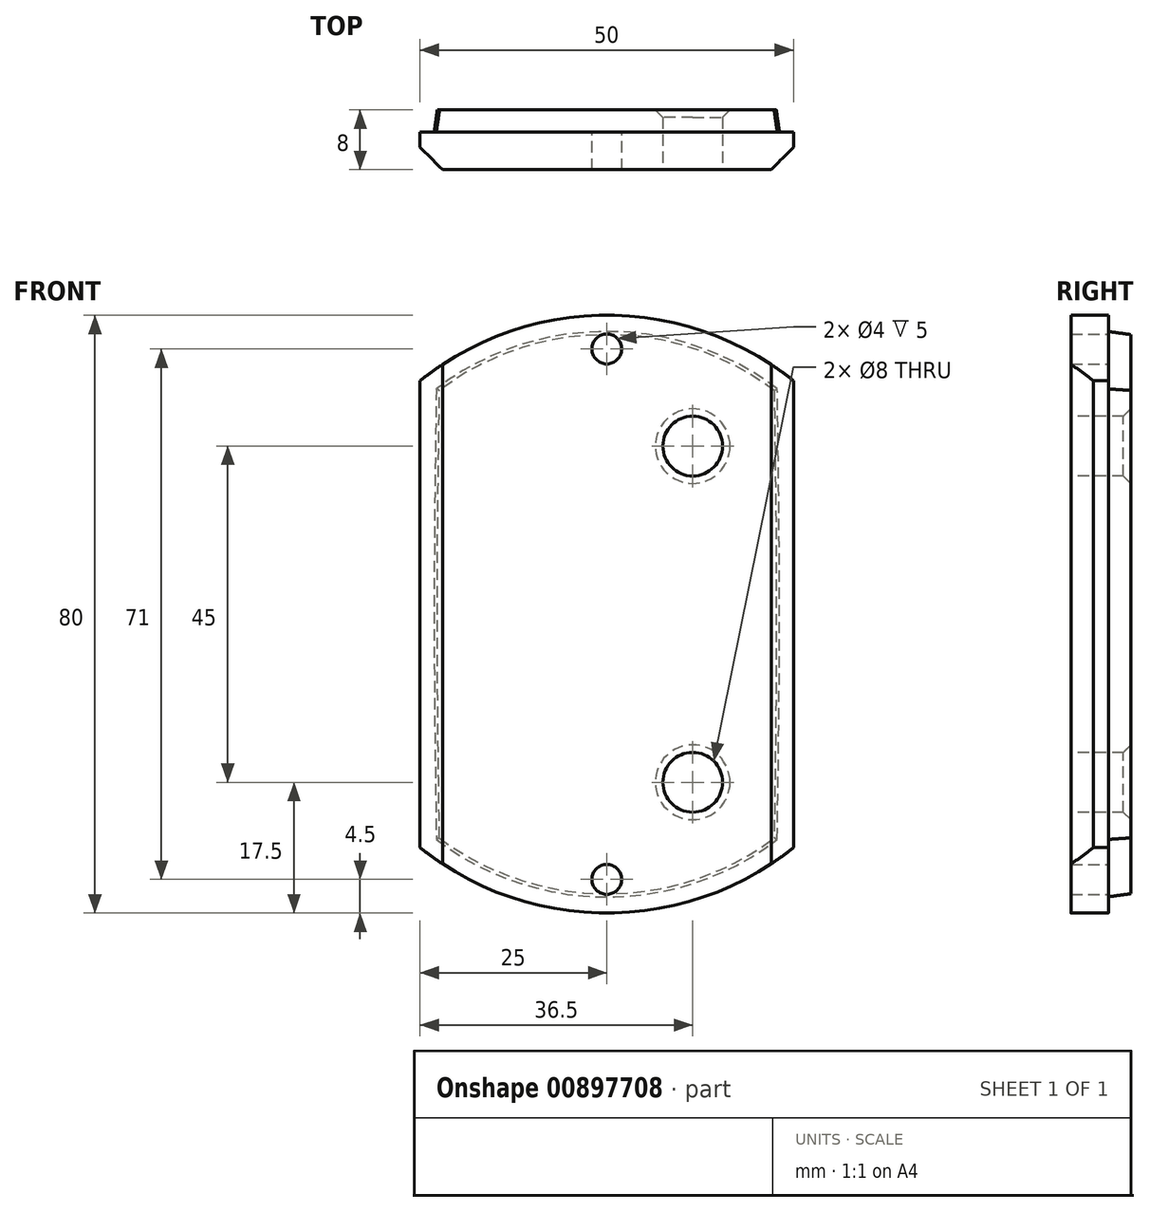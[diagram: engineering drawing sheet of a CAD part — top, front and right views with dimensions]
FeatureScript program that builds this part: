
annotation { "Feature Type Name" : "Feature", "Feature Type Description" : "" }
export const myFeature = defineFeature(function(context is Context, id is Id, definition is map)
    precondition{}
    {
        {
            var Q0;
            Q0=qCreatedBy(makeId("Front.planeOp"),FACE);
            var sketch = newSketch(context, id + "F0", { "sketchPlane" : qUnion([Q0])});
            skFitSpline(sketch, "E0.0", {"points": [v(-22.81, -30.15) * mm, v(-22, -30.77) * mm, v(-20.31, -31.94) * mm, v(-17.68, -33.47) * mm, v(-15.39, -34.57) * mm, v(-13.5, -35.33) * mm, v(-12.05, -35.85) * mm, v(-10.57, -36.32) * mm, v(-8.6, -36.85) * mm, v(-6.11, -37.36) * mm, v(-3.09, -37.73) * mm, v(-0.54, -37.84) * mm, v(1.52, -37.8) * mm, v(3.57, -37.67) * mm, v(6.1, -37.36) * mm, v(9.08, -36.75) * mm, v(12, -35.9) * mm, v(14.9, -34.8) * mm, v(17.67, -33.48) * mm, v(20.31, -31.94) * mm, v(22, -30.77) * mm, v(22.81, -30.15) * mm]});
            skLineSegment(sketch, "E1.0", {"start": v(4, -36) * mm, "end": v(4, -37.6) * mm});
            skArc(sketch, "E2.0", {"start": v(4, -36) * mm, "mid": v(0, -32) * mm, "end": v(-4, -36) * mm});
            skCircle(sketch, "E3.0", {"center": v(0, -35.5) * mm, "radius": 2 * mm});
            skLineSegment(sketch, "E4.0", {"start": v(-4, -36) * mm, "end": v(-4, -37.6) * mm});
            skFitSpline(sketch, "E5.0", {"points": [v(-22.81, -30.15) * mm, v(-22, -30.77) * mm, v(-20.31, -31.94) * mm, v(-17.68, -33.47) * mm, v(-15.39, -34.57) * mm, v(-13.5, -35.33) * mm, v(-12.05, -35.85) * mm, v(-10.57, -36.32) * mm, v(-8.6, -36.85) * mm, v(-6.11, -37.36) * mm, v(-3.09, -37.73) * mm, v(-0.54, -37.84) * mm, v(1.52, -37.8) * mm, v(3.57, -37.67) * mm, v(6.1, -37.36) * mm, v(9.08, -36.75) * mm, v(12, -35.9) * mm, v(14.9, -34.8) * mm, v(17.67, -33.48) * mm, v(20.31, -31.94) * mm, v(22, -30.77) * mm, v(22.81, -30.15) * mm]});
            skFitSpline(sketch, "E6.0", {"points": [v(-22.81, 30.15) * mm, v(-23.07, 10.05) * mm, v(-23.07, -10.05) * mm, v(-22.81, -30.15) * mm]});
            skLineSegment(sketch, "E7.0", {"start": v(-25, 31.22) * mm, "end": v(-25, -31.22) * mm});
            skFitSpline(sketch, "E8.0", {"points": [v(-25, -31.22) * mm, v(-24.12, -31.93) * mm, v(-23.21, -32.6) * mm, v(-22.28, -33.22) * mm, v(-21.34, -33.85) * mm, v(-20.38, -34.43) * mm, v(-19.4, -34.98) * mm, v(-18.42, -35.53) * mm, v(-17.4, -36.03) * mm, v(-16.38, -36.5) * mm, v(-15.36, -36.95) * mm, v(-14.31, -37.37) * mm, v(-13.25, -37.74) * mm, v(-12.19, -38.12) * mm, v(-11.1, -38.44) * mm, v(-10.02, -38.72) * mm, v(-8.93, -39) * mm, v(-7.83, -39.24) * mm, v(-6.72, -39.43) * mm, v(-5.6, -39.62) * mm, v(-4.5, -39.76) * mm, v(-3.37, -39.86) * mm, v(-2.25, -39.95) * mm, v(-1.13, -40) * mm, v(0, -40) * mm, v(1.13, -40) * mm, v(2.25, -39.95) * mm, v(3.37, -39.86) * mm, v(4.5, -39.76) * mm, v(5.6, -39.62) * mm, v(6.72, -39.43) * mm, v(7.83, -39.24) * mm, v(8.93, -39) * mm, v(10.02, -38.72) * mm, v(11.1, -38.44) * mm, v(12.18, -38.12) * mm, v(13.25, -37.74) * mm, v(14.3, -37.37) * mm, v(15.35, -36.95) * mm, v(16.38, -36.5) * mm, v(17.4, -36.03) * mm, v(18.41, -35.53) * mm, v(19.4, -34.98) * mm, v(20.38, -34.43) * mm, v(21.34, -33.85) * mm, v(22.28, -33.22) * mm, v(23.21, -32.6) * mm, v(24.12, -31.93) * mm, v(25, -31.22) * mm]});
            skLineSegment(sketch, "E9.0", {"start": v(25, -31.22) * mm, "end": v(25, 31.22) * mm});
            skFitSpline(sketch, "E10.0", {"points": [v(22.81, -30.15) * mm, v(23.07, -10.05) * mm, v(23.07, 10.05) * mm, v(22.81, 30.15) * mm]});
            skFitSpline(sketch, "E11.0", {"points": [v(22.81, 30.15) * mm, v(22, 30.77) * mm, v(20.31, 31.94) * mm, v(17.68, 33.47) * mm, v(15.39, 34.57) * mm, v(13.5, 35.33) * mm, v(12.05, 35.85) * mm, v(10.57, 36.32) * mm, v(8.6, 36.85) * mm, v(6.11, 37.36) * mm, v(3.09, 37.73) * mm, v(0.54, 37.84) * mm, v(-1.52, 37.8) * mm, v(-3.57, 37.67) * mm, v(-6.1, 37.36) * mm, v(-9.08, 36.75) * mm, v(-12, 35.9) * mm, v(-14.9, 34.8) * mm, v(-17.67, 33.48) * mm, v(-20.31, 31.94) * mm, v(-22, 30.77) * mm, v(-22.81, 30.15) * mm]});
            skFitSpline(sketch, "E12.0", {"points": [v(22.81, 30.15) * mm, v(22, 30.77) * mm, v(20.31, 31.94) * mm, v(17.68, 33.47) * mm, v(15.39, 34.57) * mm, v(13.5, 35.33) * mm, v(12.05, 35.85) * mm, v(10.57, 36.32) * mm, v(8.6, 36.85) * mm, v(6.11, 37.36) * mm, v(3.09, 37.73) * mm, v(0.54, 37.84) * mm, v(-1.52, 37.8) * mm, v(-3.57, 37.67) * mm, v(-6.1, 37.36) * mm, v(-9.08, 36.75) * mm, v(-12, 35.9) * mm, v(-14.9, 34.8) * mm, v(-17.67, 33.48) * mm, v(-20.31, 31.94) * mm, v(-22, 30.77) * mm, v(-22.81, 30.15) * mm]});
            skLineSegment(sketch, "E13.0", {"start": v(4, 36) * mm, "end": v(4, 37.6) * mm});
            skArc(sketch, "E14.0", {"start": v(4, 36) * mm, "mid": v(0, 32) * mm, "end": v(-4, 36) * mm});
            skLineSegment(sketch, "E15.0", {"start": v(-4, 36) * mm, "end": v(-4, 37.6) * mm});
            skCircle(sketch, "E16.0", {"center": v(0, 35.5) * mm, "radius": 2 * mm});
            skFitSpline(sketch, "E17.0", {"points": [v(25, 31.22) * mm, v(24.12, 31.93) * mm, v(23.21, 32.6) * mm, v(22.28, 33.22) * mm, v(21.34, 33.85) * mm, v(20.38, 34.43) * mm, v(19.4, 34.98) * mm, v(18.42, 35.53) * mm, v(17.4, 36.03) * mm, v(16.38, 36.5) * mm, v(15.36, 36.95) * mm, v(14.31, 37.37) * mm, v(13.25, 37.74) * mm, v(12.19, 38.12) * mm, v(11.1, 38.44) * mm, v(10.02, 38.72) * mm, v(8.93, 39) * mm, v(7.83, 39.24) * mm, v(6.72, 39.43) * mm, v(5.6, 39.62) * mm, v(4.5, 39.76) * mm, v(3.37, 39.86) * mm, v(2.25, 39.95) * mm, v(1.13, 40) * mm, v(0, 40) * mm, v(-1.13, 40) * mm, v(-2.25, 39.95) * mm, v(-3.37, 39.86) * mm, v(-4.5, 39.76) * mm, v(-5.6, 39.62) * mm, v(-6.72, 39.43) * mm, v(-7.83, 39.24) * mm, v(-8.93, 39) * mm, v(-10.02, 38.72) * mm, v(-11.1, 38.44) * mm, v(-12.18, 38.12) * mm, v(-13.25, 37.74) * mm, v(-14.3, 37.37) * mm, v(-15.35, 36.95) * mm, v(-16.38, 36.5) * mm, v(-17.4, 36.03) * mm, v(-18.41, 35.53) * mm, v(-19.4, 34.98) * mm, v(-20.38, 34.43) * mm, v(-21.34, 33.85) * mm, v(-22.28, 33.22) * mm, v(-23.21, 32.6) * mm, v(-24.12, 31.93) * mm, v(-25, 31.22) * mm]});
            skFitSpline(sketch, "E18.0.1", {"points": [v(-25, -31.22) * mm, v(-24.12, -31.93) * mm, v(-23.21, -32.6) * mm, v(-22.28, -33.22) * mm, v(-21.34, -33.85) * mm, v(-20.38, -34.43) * mm, v(-19.4, -34.98) * mm, v(-18.42, -35.53) * mm, v(-17.4, -36.03) * mm, v(-16.38, -36.5) * mm, v(-15.36, -36.95) * mm, v(-14.31, -37.37) * mm, v(-13.25, -37.74) * mm, v(-12.19, -38.12) * mm, v(-11.1, -38.44) * mm, v(-10.02, -38.72) * mm, v(-8.93, -39) * mm, v(-7.83, -39.24) * mm, v(-6.72, -39.43) * mm, v(-5.6, -39.62) * mm, v(-4.5, -39.76) * mm, v(-3.37, -39.86) * mm, v(-2.25, -39.95) * mm, v(-1.13, -40) * mm, v(0, -40) * mm, v(1.13, -40) * mm, v(2.25, -39.95) * mm, v(3.37, -39.86) * mm, v(4.5, -39.76) * mm, v(5.6, -39.62) * mm, v(6.72, -39.43) * mm, v(7.83, -39.24) * mm, v(8.93, -39) * mm, v(10.02, -38.72) * mm, v(11.1, -38.44) * mm, v(12.18, -38.12) * mm, v(13.25, -37.74) * mm, v(14.3, -37.37) * mm, v(15.35, -36.95) * mm, v(16.38, -36.5) * mm, v(17.4, -36.03) * mm, v(18.41, -35.53) * mm, v(19.4, -34.98) * mm, v(20.38, -34.43) * mm, v(21.34, -33.85) * mm, v(22.28, -33.22) * mm, v(23.21, -32.6) * mm, v(24.12, -31.93) * mm, v(25, -31.22) * mm]});
            skFitSpline(sketch, "E18.0.3", {"points": [v(25, 31.22) * mm, v(24.12, 31.93) * mm, v(23.21, 32.6) * mm, v(22.28, 33.22) * mm, v(21.34, 33.85) * mm, v(20.38, 34.43) * mm, v(19.4, 34.98) * mm, v(18.42, 35.53) * mm, v(17.4, 36.03) * mm, v(16.38, 36.5) * mm, v(15.36, 36.95) * mm, v(14.31, 37.37) * mm, v(13.25, 37.74) * mm, v(12.19, 38.12) * mm, v(11.1, 38.44) * mm, v(10.02, 38.72) * mm, v(8.93, 39) * mm, v(7.83, 39.24) * mm, v(6.72, 39.43) * mm, v(5.6, 39.62) * mm, v(4.5, 39.76) * mm, v(3.37, 39.86) * mm, v(2.25, 39.95) * mm, v(1.13, 40) * mm, v(0, 40) * mm, v(-1.13, 40) * mm, v(-2.25, 39.95) * mm, v(-3.37, 39.86) * mm, v(-4.5, 39.76) * mm, v(-5.6, 39.62) * mm, v(-6.72, 39.43) * mm, v(-7.83, 39.24) * mm, v(-8.93, 39) * mm, v(-10.02, 38.72) * mm, v(-11.1, 38.44) * mm, v(-12.18, 38.12) * mm, v(-13.25, 37.74) * mm, v(-14.3, 37.37) * mm, v(-15.35, 36.95) * mm, v(-16.38, 36.5) * mm, v(-17.4, 36.03) * mm, v(-18.41, 35.53) * mm, v(-19.4, 34.98) * mm, v(-20.38, 34.43) * mm, v(-21.34, 33.85) * mm, v(-22.28, 33.22) * mm, v(-23.21, 32.6) * mm, v(-24.12, 31.93) * mm, v(-25, 31.22) * mm]});
            skSolve(sketch);
        }
        {
            var Q0;
            Q0=makeQuery(id+"F0.imprint","IMPRINT",FACE,{"disambiguationData":[TD([[makeQuery(id+"F0.imprint","IMPRINT",EDGE,{"derivedFrom":sQuery(id+"F0.wireOp",EDGE,"E0.0")}),-1.0]])]});
            var Q1;
            Q1=makeQuery(id+"F0.imprint","IMPRINT",FACE,{"disambiguationData":[TD([[makeQuery(id+"F0.imprint","IMPRINT",EDGE,{"derivedFrom":sQuery(id+"F0.wireOp",EDGE,"E0.0")}),1.0]])]});
            extrude(context, id + "F1", {"entities" : qUnion([Q0, Q1]), "depth" : 5 * mm, "offsetDistance" : 25 * mm});
        }
        {
            var Q0;
            Q0=makeQuery(id+"F1.opExtrude","CAP_FACE",FACE,{"disambiguationData":[OSD([sQuery(id+"F0.wireOp",EDGE,"E3.0"),sQuery(id+"F0.wireOp",EDGE,"E16.0"),sQuery(id+"F0.wireOp",EDGE,"E7.0"),sQuery(id+"F0.wireOp",EDGE,"E18.0.1"),sQuery(id+"F0.wireOp",EDGE,"E9.0"),sQuery(id+"F0.wireOp",EDGE,"E18.0.3")])],"isStart":true});
            var sketch = newSketch(context, id + "F2", { "sketchPlane" : qUnion([Q0])});
            skFitSpline(sketch, "E19.0", {"points": [v(22.81, 30.15) * mm, v(23.07, 10.05) * mm, v(23.07, -10.05) * mm, v(22.81, -30.15) * mm]});
            skFitSpline(sketch, "E20.0", {"points": [v(-22.81, 30.15) * mm, v(-22, 30.77) * mm, v(-20.31, 31.94) * mm, v(-17.68, 33.47) * mm, v(-15.39, 34.57) * mm, v(-13.5, 35.33) * mm, v(-12.05, 35.85) * mm, v(-10.57, 36.32) * mm, v(-8.6, 36.85) * mm, v(-6.11, 37.36) * mm, v(-3.09, 37.73) * mm, v(-0.54, 37.84) * mm, v(1.52, 37.8) * mm, v(3.57, 37.67) * mm, v(6.1, 37.36) * mm, v(9.08, 36.75) * mm, v(12, 35.9) * mm, v(14.9, 34.8) * mm, v(17.67, 33.48) * mm, v(20.31, 31.94) * mm, v(22, 30.77) * mm, v(22.81, 30.15) * mm]});
            skLineSegment(sketch, "E21.0", {"start": v(4, 36) * mm, "end": v(4, 37.6) * mm});
            skArc(sketch, "E22.0", {"start": v(-4, 36) * mm, "mid": v(0, 32) * mm, "end": v(4, 36) * mm});
            skLineSegment(sketch, "E23.0", {"start": v(-4, 36) * mm, "end": v(-4, 37.6) * mm});
            skFitSpline(sketch, "E24.0", {"points": [v(-22.81, 30.15) * mm, v(-22, 30.77) * mm, v(-20.31, 31.94) * mm, v(-17.68, 33.47) * mm, v(-15.39, 34.57) * mm, v(-13.5, 35.33) * mm, v(-12.05, 35.85) * mm, v(-10.57, 36.32) * mm, v(-8.6, 36.85) * mm, v(-6.11, 37.36) * mm, v(-3.09, 37.73) * mm, v(-0.54, 37.84) * mm, v(1.52, 37.8) * mm, v(3.57, 37.67) * mm, v(6.1, 37.36) * mm, v(9.08, 36.75) * mm, v(12, 35.9) * mm, v(14.9, 34.8) * mm, v(17.67, 33.48) * mm, v(20.31, 31.94) * mm, v(22, 30.77) * mm, v(22.81, 30.15) * mm]});
            skFitSpline(sketch, "E25.0", {"points": [v(-22.81, -30.15) * mm, v(-23.07, -10.05) * mm, v(-23.07, 10.05) * mm, v(-22.81, 30.15) * mm]});
            skFitSpline(sketch, "E26.0", {"points": [v(22.81, -30.15) * mm, v(22, -30.77) * mm, v(20.31, -31.94) * mm, v(17.68, -33.47) * mm, v(15.39, -34.57) * mm, v(13.5, -35.33) * mm, v(12.05, -35.85) * mm, v(10.57, -36.32) * mm, v(8.6, -36.85) * mm, v(6.11, -37.36) * mm, v(3.09, -37.73) * mm, v(0.54, -37.84) * mm, v(-1.52, -37.8) * mm, v(-3.57, -37.67) * mm, v(-6.1, -37.36) * mm, v(-9.08, -36.75) * mm, v(-12, -35.9) * mm, v(-14.9, -34.8) * mm, v(-17.67, -33.48) * mm, v(-20.31, -31.94) * mm, v(-22, -30.77) * mm, v(-22.81, -30.15) * mm]});
            skLineSegment(sketch, "E27.0", {"start": v(-4, -36) * mm, "end": v(-4, -37.6) * mm});
            skArc(sketch, "E28.0", {"start": v(-4, -36) * mm, "mid": v(0, -32) * mm, "end": v(4, -36) * mm});
            skLineSegment(sketch, "E29.0", {"start": v(4, -36) * mm, "end": v(4, -37.6) * mm});
            skFitSpline(sketch, "E30.0", {"points": [v(22.81, -30.15) * mm, v(22, -30.77) * mm, v(20.31, -31.94) * mm, v(17.68, -33.47) * mm, v(15.39, -34.57) * mm, v(13.5, -35.33) * mm, v(12.05, -35.85) * mm, v(10.57, -36.32) * mm, v(8.6, -36.85) * mm, v(6.11, -37.36) * mm, v(3.09, -37.73) * mm, v(0.54, -37.84) * mm, v(-1.52, -37.8) * mm, v(-3.57, -37.67) * mm, v(-6.1, -37.36) * mm, v(-9.08, -36.75) * mm, v(-12, -35.9) * mm, v(-14.9, -34.8) * mm, v(-17.67, -33.48) * mm, v(-20.31, -31.94) * mm, v(-22, -30.77) * mm, v(-22.81, -30.15) * mm]});
            skSolve(sketch);
        }
        {
            var Q0;
            Q0=makeQuery(id+"F2.imprint","IMPRINT",FACE,{"disambiguationData":[TD([[makeQuery(id+"F2.imprint","IMPRINT",EDGE,{"derivedFrom":sQuery(id+"F2.wireOp",EDGE,"E19.0")}),-1.0]])]});
            extrude(context, id + "F3", {"entities" : qUnion([Q0]), "operationType" : NewBodyOperationType.ADD, "oppositeDirection" : true, "depth" : 3 * mm, "offsetDistance" : 25 * mm});
        }
        {
            var Q0;
            Q0 = qSketchRegion(id + "F2", true);
            extrude(context, id + "F4", {"entities" : qUnion([Q0]), "operationType" : NewBodyOperationType.ADD, "depth" : 3 * mm, "offsetDistance" : 25 * mm, "hasDraft" : true, "draftAngle" : 8 * degree, "draftPullDirection" : true});
        }
        {
            var Q0;
            Q0=makeQuery(id+"F1.opExtrude","CAP_EDGE",EDGE,{"disambiguationData":[OSD([sQuery(id+"F0.wireOp",EDGE,"E7.0")])],"isStart":false});
            var Q1;
            Q1=makeQuery(id+"F1.opExtrude","CAP_EDGE",EDGE,{"disambiguationData":[OSD([sQuery(id+"F0.wireOp",EDGE,"E9.0")])],"isStart":false});
            chamfer(context, id + "F5", {"entities" : qUnion([Q0, Q1]), "width" : 3 * mm, "tangentPropagation" : true});
        }
        {
            var Q0;
            Q0=makeQuery(id+"F1.opExtrude","CAP_FACE",FACE,{"disambiguationData":[OSD([sQuery(id+"F0.wireOp",EDGE,"E3.0"),sQuery(id+"F0.wireOp",EDGE,"E16.0"),sQuery(id+"F0.wireOp",EDGE,"E7.0"),sQuery(id+"F0.wireOp",EDGE,"E18.0.1"),sQuery(id+"F0.wireOp",EDGE,"E9.0"),sQuery(id+"F0.wireOp",EDGE,"E18.0.3")])],"isStart":false});
            var sketch = newSketch(context, id + "F6", { "sketchPlane" : qUnion([Q0])});
            skSolve(sketch);
        }
        {
            var Q0;
            {var subQ5=sQuery(id+"F0.wireOp",EDGE,"E3.0");Q0=makeQuery(id+"F6.imprint","IMPRINT",FACE,{"disambiguationData":[TD([[makeQuery(id+"F6.imprint","IMPRINT",EDGE,{"derivedFrom":makeQuery(id+"F1.opExtrude","CAP_EDGE",EDGE,{"disambiguationData":[OSD([subQ5])],"isStart":false})}),-1.0]])]});}
            var sketch = newSketch(context, id + "F7", { "sketchPlane" : qUnion([Q0])});
            skPoint(sketch, "E31.endSnap0", {"position": v(0, -1.15) * mm});
            skCircle(sketch, "E32", {"center": v(11.5, 22.5) * mm, "radius": 4 * mm});
            skFitSpline(sketch, "E33.0", {"points": [v(25, 31.22) * mm, v(24.12, 31.93) * mm, v(23.21, 32.6) * mm, v(22.28, 33.22) * mm, v(21.34, 33.85) * mm, v(20.38, 34.43) * mm, v(19.4, 34.98) * mm, v(18.42, 35.53) * mm, v(17.4, 36.03) * mm, v(16.38, 36.5) * mm, v(15.36, 36.95) * mm, v(14.31, 37.37) * mm, v(13.25, 37.74) * mm, v(12.19, 38.12) * mm, v(11.1, 38.44) * mm, v(10.02, 38.72) * mm, v(8.93, 39) * mm, v(7.83, 39.24) * mm, v(6.72, 39.43) * mm, v(5.6, 39.62) * mm, v(4.5, 39.76) * mm, v(3.37, 39.86) * mm, v(2.25, 39.95) * mm, v(1.13, 40) * mm, v(0, 40) * mm, v(-1.13, 40) * mm, v(-2.25, 39.95) * mm, v(-3.37, 39.86) * mm, v(-4.5, 39.76) * mm, v(-5.6, 39.62) * mm, v(-6.72, 39.43) * mm, v(-7.83, 39.24) * mm, v(-8.93, 39) * mm, v(-10.02, 38.72) * mm, v(-11.1, 38.44) * mm, v(-12.18, 38.12) * mm, v(-13.25, 37.74) * mm, v(-14.3, 37.37) * mm, v(-15.35, 36.95) * mm, v(-16.38, 36.5) * mm, v(-17.4, 36.03) * mm, v(-18.41, 35.53) * mm, v(-19.4, 34.98) * mm, v(-20.38, 34.43) * mm, v(-21.34, 33.85) * mm, v(-22.28, 33.22) * mm, v(-23.21, 32.6) * mm, v(-24.12, 31.93) * mm, v(-25, 31.22) * mm], "construction": true});
            skFitSpline(sketch, "E34.0", {"points": [v(-25, -31.22) * mm, v(-24.12, -31.93) * mm, v(-23.21, -32.6) * mm, v(-22.28, -33.22) * mm, v(-21.34, -33.85) * mm, v(-20.38, -34.43) * mm, v(-19.4, -34.98) * mm, v(-18.42, -35.53) * mm, v(-17.4, -36.03) * mm, v(-16.38, -36.5) * mm, v(-15.36, -36.95) * mm, v(-14.31, -37.37) * mm, v(-13.25, -37.74) * mm, v(-12.19, -38.12) * mm, v(-11.1, -38.44) * mm, v(-10.02, -38.72) * mm, v(-8.93, -39) * mm, v(-7.83, -39.24) * mm, v(-6.72, -39.43) * mm, v(-5.6, -39.62) * mm, v(-4.5, -39.76) * mm, v(-3.37, -39.86) * mm, v(-2.25, -39.95) * mm, v(-1.13, -40) * mm, v(0, -40) * mm, v(1.13, -40) * mm, v(2.25, -39.95) * mm, v(3.37, -39.86) * mm, v(4.5, -39.76) * mm, v(5.6, -39.62) * mm, v(6.72, -39.43) * mm, v(7.83, -39.24) * mm, v(8.93, -39) * mm, v(10.02, -38.72) * mm, v(11.1, -38.44) * mm, v(12.18, -38.12) * mm, v(13.25, -37.74) * mm, v(14.3, -37.37) * mm, v(15.35, -36.95) * mm, v(16.38, -36.5) * mm, v(17.4, -36.03) * mm, v(18.41, -35.53) * mm, v(19.4, -34.98) * mm, v(20.38, -34.43) * mm, v(21.34, -33.85) * mm, v(22.28, -33.22) * mm, v(23.21, -32.6) * mm, v(24.12, -31.93) * mm, v(25, -31.22) * mm], "construction": true});
            skLineSegment(sketch, "E35", {"start": v(0, 40) * mm, "end": v(0, -40) * mm, "construction": true});
            skLineSegment(sketch, "E36", {"start": v(11.5, 44.99) * mm, "end": v(11.5, -52.44) * mm, "construction": true});
            skLineSegment(sketch, "E37", {"start": v(-29.88, 0) * mm, "end": v(35.22, 0) * mm, "construction": true});
            skCircle(sketch, "E38.MirrorC", {"center": v(11.5, -22.5) * mm, "radius": 4 * mm});
            skSolve(sketch);
        }
        {
            var Q0;
            Q0 = qSketchRegion(id + "F7", true);
            extrude(context, id + "F8", {"entities" : qUnion([Q0]), "operationType" : NewBodyOperationType.REMOVE, "oppositeDirection" : true, "depth" : 25 * mm, "offsetDistance" : 25 * mm});
        }
        {
            var Q0;
            Q0=makeQuery(id+"F1.opExtrude","CAP_EDGE",EDGE,{"disambiguationData":[OSD([sQuery(id+"F0.wireOp",EDGE,"E18.0.3")])],"isStart":false});
            var Q1;
            Q1=makeQuery(id+"F1.opExtrude","CAP_EDGE",EDGE,{"disambiguationData":[OSD([sQuery(id+"F0.wireOp",EDGE,"E18.0.1")])],"isStart":false});
            var Q2;
            Q2=makeQuery(id+"F8.boolean.opBoolean","COPY",EDGE,{"derivedFrom":makeQuery(id+"F8.opExtrude","CAP_EDGE",EDGE,{"disambiguationData":[OSD([sQuery(id+"F7.wireOp",EDGE,"E32")])],"isStart":true})});
            var Q3;
            Q3=makeQuery(id+"F8.boolean.opBoolean","COPY",EDGE,{"derivedFrom":makeQuery(id+"F8.opExtrude","CAP_EDGE",EDGE,{"disambiguationData":[OSD([sQuery(id+"F7.wireOp",EDGE,"E38.MirrorC")])],"isStart":true})});
            var Q4;
            Q4=makeQuery(id+"F8.boolean.opBoolean","INTERSECT",EDGE,{"derivedFrom":[makeQuery(id+"F4.opExtrude","CAP_FACE",FACE,{"disambiguationData":[OSD([sQuery(id+"F2.wireOp",EDGE,"E19.0"),sQuery(id+"F2.wireOp",EDGE,"E20.0"),sQuery(id+"F2.wireOp",EDGE,"E21.0"),sQuery(id+"F2.wireOp",EDGE,"E22.0"),sQuery(id+"F2.wireOp",EDGE,"E23.0"),sQuery(id+"F2.wireOp",EDGE,"E24.0"),sQuery(id+"F2.wireOp",EDGE,"E25.0"),sQuery(id+"F2.wireOp",EDGE,"E26.0"),sQuery(id+"F2.wireOp",EDGE,"E27.0"),sQuery(id+"F2.wireOp",EDGE,"E28.0"),sQuery(id+"F2.wireOp",EDGE,"E29.0"),sQuery(id+"F2.wireOp",EDGE,"E30.0")])],"isStart":false}),makeQuery(id+"F8.opExtrude","SWEPT_FACE",FACE,{"disambiguationData":[OSD([sQuery(id+"F7.wireOp",EDGE,"E38.MirrorC")])]})]});
            var Q5;
            Q5=makeQuery(id+"F8.boolean.opBoolean","INTERSECT",EDGE,{"derivedFrom":[makeQuery(id+"F4.opExtrude","CAP_FACE",FACE,{"disambiguationData":[OSD([sQuery(id+"F2.wireOp",EDGE,"E19.0"),sQuery(id+"F2.wireOp",EDGE,"E20.0"),sQuery(id+"F2.wireOp",EDGE,"E21.0"),sQuery(id+"F2.wireOp",EDGE,"E22.0"),sQuery(id+"F2.wireOp",EDGE,"E23.0"),sQuery(id+"F2.wireOp",EDGE,"E24.0"),sQuery(id+"F2.wireOp",EDGE,"E25.0"),sQuery(id+"F2.wireOp",EDGE,"E26.0"),sQuery(id+"F2.wireOp",EDGE,"E27.0"),sQuery(id+"F2.wireOp",EDGE,"E28.0"),sQuery(id+"F2.wireOp",EDGE,"E29.0"),sQuery(id+"F2.wireOp",EDGE,"E30.0")])],"isStart":false}),makeQuery(id+"F8.opExtrude","SWEPT_FACE",FACE,{"disambiguationData":[OSD([sQuery(id+"F7.wireOp",EDGE,"E32")])]})]});
            chamfer(context, id + "F9", {"entities" : qUnion([Q0, Q1, Q2, Q3, Q4, Q5]), "width" : 1 * mm, "tangentPropagation" : true});
        }
    });
